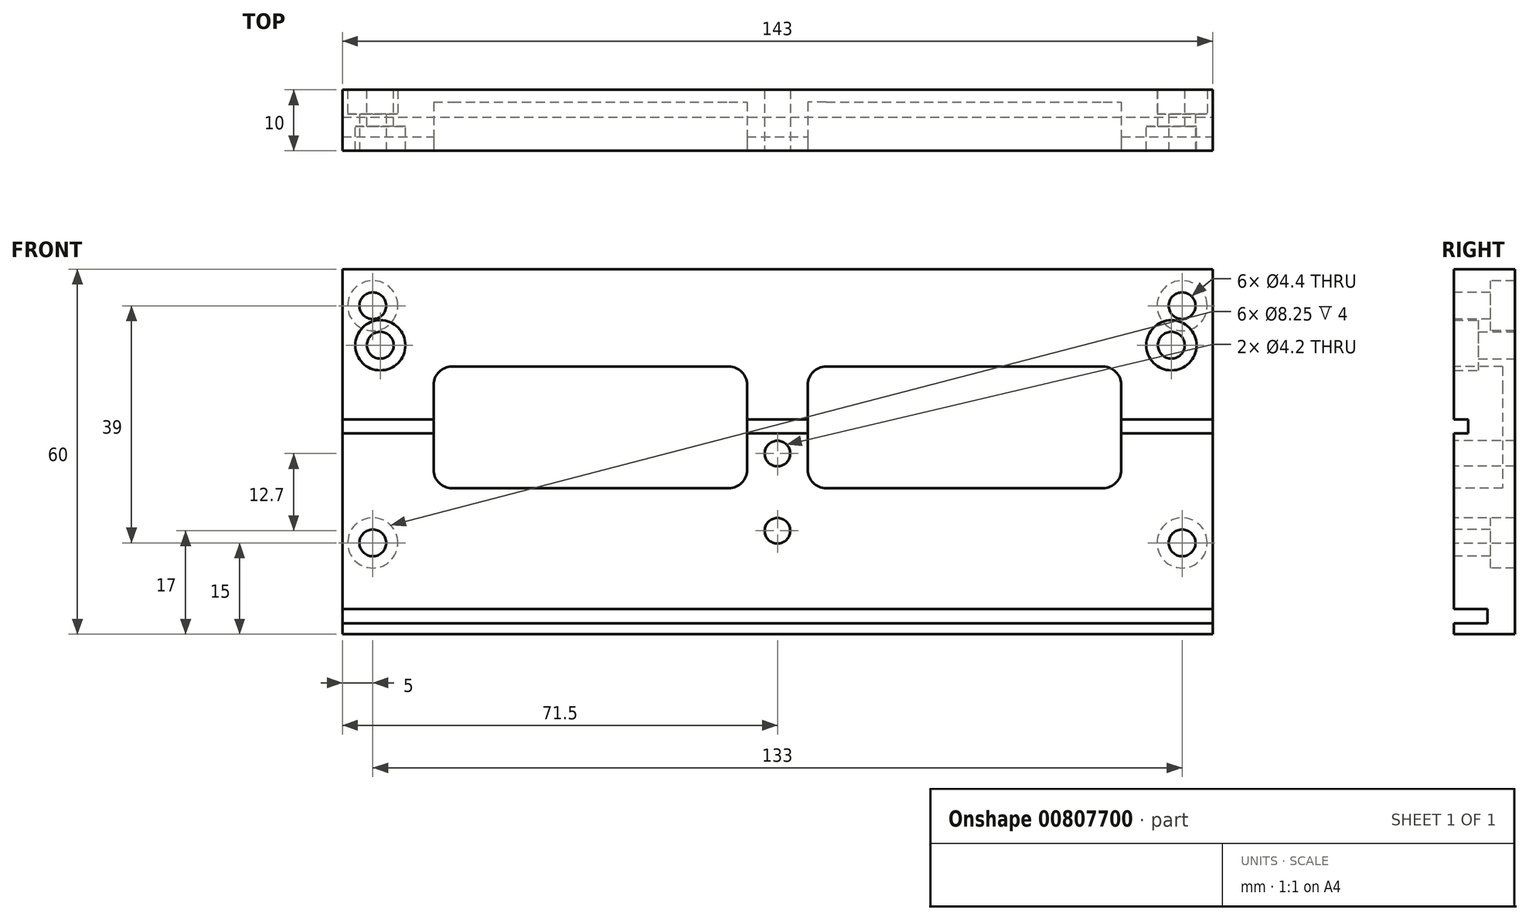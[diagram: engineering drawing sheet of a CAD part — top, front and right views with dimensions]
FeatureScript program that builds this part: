
annotation { "Feature Type Name" : "Feature", "Feature Type Description" : "" }
export const myFeature = defineFeature(function(context is Context, id is Id, definition is map)
    precondition{}
    {
        {
            var Q0;
            Q0=qCreatedBy(makeId("Front.planeOp"),FACE);
            var sketch = newSketch(context, id + "F0", { "sketchPlane" : qUnion([Q0])});
            skLineSegment(sketch, "E0.bottom", {"start": v(71.5, 30) * mm, "end": v(-71.5, 30) * mm});
            skLineSegment(sketch, "E0.top", {"start": v(71.5, -30) * mm, "end": v(-71.5, -30) * mm});
            skLineSegment(sketch, "E0.left", {"start": v(71.5, 30) * mm, "end": v(71.5, -30) * mm});
            skLineSegment(sketch, "E0.right", {"start": v(-71.5, 30) * mm, "end": v(-71.5, -30) * mm});
            skPoint(sketch, "E0.middle", {"position": v(0, 0) * mm});
            skSolve(sketch);
        }
        {
            var Q0;
            Q0 = qSketchRegion(id + "F0", true);
            extrude(context, id + "F1", {"entities" : qUnion([Q0]), "depth" : 10 * mm, "offsetDistance" : 25 * mm});
        }
        {
            var Q0;
            Q0=makeQuery(id+"F1.opExtrude","CAP_FACE",FACE,{"disambiguationData":[OSD([sQuery(id+"F0.wireOp",EDGE,"E0.bottom"),sQuery(id+"F0.wireOp",EDGE,"E0.top"),sQuery(id+"F0.wireOp",EDGE,"E0.left"),sQuery(id+"F0.wireOp",EDGE,"E0.right")])],"isStart":false});
            var sketch = newSketch(context, id + "F2", { "sketchPlane" : qUnion([Q0])});
            skLineSegment(sketch, "E1.bottom", {"start": v(-56.5, 14) * mm, "end": v(-5, 14) * mm});
            skLineSegment(sketch, "E1.top", {"start": v(-56.5, -6) * mm, "end": v(-5, -6) * mm});
            skLineSegment(sketch, "E1.left", {"start": v(-56.5, 14) * mm, "end": v(-56.5, -6) * mm});
            skLineSegment(sketch, "E1.right", {"start": v(-5, 14) * mm, "end": v(-5, -6) * mm});
            skLineSegment(sketch, "E2.bottom", {"start": v(5, 14) * mm, "end": v(56.5, 14) * mm});
            skLineSegment(sketch, "E2.top", {"start": v(5, -6) * mm, "end": v(56.5, -6) * mm});
            skLineSegment(sketch, "E2.left", {"start": v(5, 14) * mm, "end": v(5, -6) * mm});
            skLineSegment(sketch, "E2.right", {"start": v(56.5, 14) * mm, "end": v(56.5, -6) * mm});
            skPoint(sketch, "E3", {"position": v(0, -14.26) * mm});
            skPoint(sketch, "E4", {"position": v(0, 15.54) * mm});
            skSolve(sketch);
        }
        {
            var Q0;
            Q0 = qSketchRegion(id + "F2", true);
            extrude(context, id + "F3", {"entities" : qUnion([Q0]), "operationType" : NewBodyOperationType.REMOVE, "oppositeDirection" : true, "depth" : 8 * mm, "offsetDistance" : 25 * mm});
        }
        {
            var Q0;
            Q0=makeQuery(id+"F3.boolean.opBoolean","COPY",EDGE,{"derivedFrom":makeQuery(id+"F3.opExtrude","SWEPT_EDGE",EDGE,{"disambiguationData":[OSD([sQuery(id+"F2.wireOp",EDGE,"E1.bottom"),sQuery(id+"F2.wireOp",EDGE,"E1.left")])]})});
            var Q1;
            Q1=makeQuery(id+"F3.boolean.opBoolean","COPY",EDGE,{"derivedFrom":makeQuery(id+"F3.opExtrude","SWEPT_EDGE",EDGE,{"disambiguationData":[OSD([sQuery(id+"F2.wireOp",EDGE,"E1.top"),sQuery(id+"F2.wireOp",EDGE,"E1.right")])]})});
            var Q2;
            Q2=makeQuery(id+"F3.boolean.opBoolean","COPY",EDGE,{"derivedFrom":makeQuery(id+"F3.opExtrude","SWEPT_EDGE",EDGE,{"disambiguationData":[OSD([sQuery(id+"F2.wireOp",EDGE,"E2.top"),sQuery(id+"F2.wireOp",EDGE,"E2.right")])]})});
            var Q3;
            Q3=makeQuery(id+"F3.boolean.opBoolean","COPY",EDGE,{"derivedFrom":makeQuery(id+"F3.opExtrude","SWEPT_EDGE",EDGE,{"disambiguationData":[OSD([sQuery(id+"F2.wireOp",EDGE,"E1.bottom"),sQuery(id+"F2.wireOp",EDGE,"E1.right")])]})});
            var Q4;
            Q4=makeQuery(id+"F3.boolean.opBoolean","COPY",EDGE,{"derivedFrom":makeQuery(id+"F3.opExtrude","SWEPT_EDGE",EDGE,{"disambiguationData":[OSD([sQuery(id+"F2.wireOp",EDGE,"E2.bottom"),sQuery(id+"F2.wireOp",EDGE,"E2.right")])]})});
            var Q5;
            Q5=makeQuery(id+"F3.boolean.opBoolean","COPY",EDGE,{"derivedFrom":makeQuery(id+"F3.opExtrude","SWEPT_EDGE",EDGE,{"disambiguationData":[OSD([sQuery(id+"F2.wireOp",EDGE,"E1.top"),sQuery(id+"F2.wireOp",EDGE,"E1.left")])]})});
            var Q6;
            Q6=makeQuery(id+"F3.boolean.opBoolean","COPY",EDGE,{"derivedFrom":makeQuery(id+"F3.opExtrude","SWEPT_EDGE",EDGE,{"disambiguationData":[OSD([sQuery(id+"F2.wireOp",EDGE,"E2.top"),sQuery(id+"F2.wireOp",EDGE,"E2.left")])]})});
            var Q7;
            Q7=makeQuery(id+"F3.boolean.opBoolean","COPY",EDGE,{"derivedFrom":makeQuery(id+"F3.opExtrude","SWEPT_EDGE",EDGE,{"disambiguationData":[OSD([sQuery(id+"F2.wireOp",EDGE,"E2.bottom"),sQuery(id+"F2.wireOp",EDGE,"E2.left")])]})});
            fillet(context, id + "F4", {"entities" : qUnion([Q0, Q1, Q2, Q3, Q4, Q5, Q6, Q7]), "radius" : 3 * mm, "tangentPropagation" : true, "allowEdgeOverflow" : false});
        }
        {
            var Q0;
            Q0=makeQuery(id+"F1.opExtrude","CAP_FACE",FACE,{"disambiguationData":[OSD([sQuery(id+"F0.wireOp",EDGE,"E0.bottom"),sQuery(id+"F0.wireOp",EDGE,"E0.top"),sQuery(id+"F0.wireOp",EDGE,"E0.left"),sQuery(id+"F0.wireOp",EDGE,"E0.right")])],"isStart":false});
            var sketch = newSketch(context, id + "F5", { "sketchPlane" : qUnion([Q0])});
            skLineSegment(sketch, "E5.bottom", {"start": v(-71.5, -25.9) * mm, "end": v(71.5, -25.9) * mm});
            skLineSegment(sketch, "E5.top", {"start": v(-71.5, -28.2) * mm, "end": v(71.5, -28.2) * mm});
            skLineSegment(sketch, "E5.left", {"start": v(-71.5, -25.9) * mm, "end": v(-71.5, -28.2) * mm});
            skLineSegment(sketch, "E5.right", {"start": v(71.5, -25.9) * mm, "end": v(71.5, -28.2) * mm});
            skSolve(sketch);
        }
        {
            var Q0;
            Q0 = qSketchRegion(id + "F5", true);
            extrude(context, id + "F6", {"entities" : qUnion([Q0]), "operationType" : NewBodyOperationType.REMOVE, "oppositeDirection" : true, "depth" : 5.5 * mm, "offsetDistance" : 25 * mm});
        }
        {
            var Q0;
            {var subQ6=sQuery(id+"F0.wireOp",EDGE,"E0.bottom");var subQ8=sQuery(id+"F0.wireOp",EDGE,"E0.left");var subQ10=sQuery(id+"F0.wireOp",EDGE,"E0.right");Q0=makeQuery(id+"F6.boolean.opBoolean","SPLIT",FACE,{"disambiguationData":[TD([makeQuery(id+"F1.opExtrude","SWEPT_FACE",FACE,{"disambiguationData":[OSD([subQ6])]})])],"derivedFrom":makeQuery(id+"F1.opExtrude","CAP_FACE",FACE,{"disambiguationData":[OSD([subQ6,sQuery(id+"F0.wireOp",EDGE,"E0.top"),subQ8,subQ10])],"isStart":false})});}
            var sketch = newSketch(context, id + "F7", { "sketchPlane" : qUnion([Q0])});
            skLineSegment(sketch, "E6.bottom", {"start": v(-71.5, 5.3) * mm, "end": v(71.5, 5.3) * mm});
            skLineSegment(sketch, "E6.top", {"start": v(-71.5, 3) * mm, "end": v(71.5, 3) * mm});
            skLineSegment(sketch, "E6.left", {"start": v(-71.5, 5.3) * mm, "end": v(-71.5, 3) * mm});
            skLineSegment(sketch, "E6.right", {"start": v(71.5, 5.3) * mm, "end": v(71.5, 3) * mm});
            skSolve(sketch);
        }
        {
            var Q0;
            Q0 = qSketchRegion(id + "F7", true);
            extrude(context, id + "F8", {"entities" : qUnion([Q0]), "operationType" : NewBodyOperationType.REMOVE, "oppositeDirection" : true, "depth" : 2.3 * mm, "offsetDistance" : 25 * mm});
        }
        {
            var Q0;
            Q0=makeQuery(id+"F1.opExtrude","CAP_FACE",FACE,{"disambiguationData":[OSD([sQuery(id+"F0.wireOp",EDGE,"E0.bottom"),sQuery(id+"F0.wireOp",EDGE,"E0.top"),sQuery(id+"F0.wireOp",EDGE,"E0.left"),sQuery(id+"F0.wireOp",EDGE,"E0.right")])],"isStart":true});
            var sketch = newSketch(context, id + "F9", { "sketchPlane" : qUnion([Q0])});
            skPoint(sketch, "E7", {"position": v(-66.5, 24) * mm});
            skPoint(sketch, "E8", {"position": v(-66.5, -15) * mm});
            skPoint(sketch, "E9", {"position": v(66.5, -15) * mm});
            skPoint(sketch, "E10", {"position": v(66.5, 24) * mm});
            skSolve(sketch);
        }
        {
            var Q0;
            Q0=sQuery(id+"F9.wireOp",VERTEX,"E7");
            var Q1;
            Q1=sQuery(id+"F9.wireOp",VERTEX,"E8");
            var Q2;
            Q2=sQuery(id+"F9.wireOp",VERTEX,"E9");
            var Q3;
            Q3=sQuery(id+"F9.wireOp",VERTEX,"E10");
            var Q4;
            Q4=makeQuery(id+"F1.opExtrude","SWEPT_BODY",BODY,{"disambiguationData":[OSD([sQuery(id+"F0.wireOp",EDGE,"E0.bottom"),sQuery(id+"F0.wireOp",EDGE,"E0.top"),sQuery(id+"F0.wireOp",EDGE,"E0.left"),sQuery(id+"F0.wireOp",EDGE,"E0.right")])]});
            hole(context, id + "F10", {"style" : HoleStyle.C_BORE, "endStyle" : HoleEndStyle.THROUGH, "standardTappedOrClearance" : lookupTablePath({ "standard" : "ISO", "fit" : "Normal", "size" : "M4", "type" : "Clearance" }), "standardBlindInLast" : lookupTablePath({ "fit" : "Standard", "standard" : "ISO", "size" : "M4", "type" : "Clearance" }), "holeDiameter" : 4.4 * mm, "cBoreDiameter" : 8.25 * mm, "cBoreDepth" : 4 * mm, "majorDiameter" : 5 * mm, "tappedDepth" : 20 * mm, "tapClearance" : 3, "locations" : qUnion([Q0, Q1, Q2, Q3]), "scope" : qUnion([Q4]), "startStyle" : HoleStartStyle.PART});
        }
        {
            var Q0;
            {var subQ12=sQuery(id+"F0.wireOp",EDGE,"E0.bottom");var subQ13=makeQuery(id+"F1.opExtrude","SWEPT_FACE",FACE,{"disambiguationData":[OSD([subQ12])]});var subQ15=sQuery(id+"F0.wireOp",EDGE,"E0.left");var subQ18=sQuery(id+"F0.wireOp",EDGE,"E0.right");Q0=makeQuery(id+"F8.boolean.opBoolean","SPLIT",FACE,{"disambiguationData":[TD([subQ13])],"derivedFrom":makeQuery(id+"F6.boolean.opBoolean","SPLIT",FACE,{"disambiguationData":[TD([subQ13])],"derivedFrom":makeQuery(id+"F1.opExtrude","CAP_FACE",FACE,{"disambiguationData":[OSD([subQ12,sQuery(id+"F0.wireOp",EDGE,"E0.top"),subQ15,subQ18])],"isStart":false})})});}
            var sketch = newSketch(context, id + "F11", { "sketchPlane" : qUnion([Q0])});
            skPoint(sketch, "E11", {"position": v(-65.27, 17.5) * mm});
            skPoint(sketch, "E12", {"position": v(64.73, 17.5) * mm});
            skSolve(sketch);
        }
        {
            var Q0;
            Q0=sQuery(id+"F11.wireOp",VERTEX,"E11");
            var Q1;
            Q1=sQuery(id+"F11.wireOp",VERTEX,"E12");
            var Q2;
            Q2=makeQuery(id+"F1.opExtrude","SWEPT_BODY",BODY,{"disambiguationData":[OSD([sQuery(id+"F0.wireOp",EDGE,"E0.bottom"),sQuery(id+"F0.wireOp",EDGE,"E0.top"),sQuery(id+"F0.wireOp",EDGE,"E0.left"),sQuery(id+"F0.wireOp",EDGE,"E0.right")])]});
            hole(context, id + "F12", {"style" : HoleStyle.C_BORE, "endStyle" : HoleEndStyle.THROUGH, "standardTappedOrClearance" : lookupTablePath({ "standard" : "ISO", "fit" : "Normal", "size" : "M4", "type" : "Clearance" }), "standardBlindInLast" : lookupTablePath({ "fit" : "Standard", "standard" : "ISO", "size" : "M4", "type" : "Clearance" }), "holeDiameter" : 4.4 * mm, "cBoreDiameter" : 8.25 * mm, "cBoreDepth" : 4 * mm, "majorDiameter" : 5 * mm, "tappedDepth" : 20 * mm, "tapClearance" : 3, "locations" : qUnion([Q0, Q1]), "scope" : qUnion([Q2]), "startStyle" : HoleStartStyle.PART});
        }
        {
            var Q0;
            Q0=makeQuery(id+"F1.opExtrude","CAP_FACE",FACE,{"disambiguationData":[OSD([sQuery(id+"F0.wireOp",EDGE,"E0.bottom"),sQuery(id+"F0.wireOp",EDGE,"E0.top"),sQuery(id+"F0.wireOp",EDGE,"E0.left"),sQuery(id+"F0.wireOp",EDGE,"E0.right")])],"isStart":true});
            var sketch = newSketch(context, id + "F13", { "sketchPlane" : qUnion([Q0])});
            skPoint(sketch, "E13", {"position": v(0, -0.3) * mm});
            skPoint(sketch, "E14", {"position": v(0, -13) * mm});
            skSolve(sketch);
        }
        {
            var Q0;
            Q0=sQuery(id+"F13.wireOp",VERTEX,"E13");
            var Q1;
            Q1=sQuery(id+"F13.wireOp",VERTEX,"E14");
            var Q2;
            Q2=makeQuery(id+"F1.opExtrude","SWEPT_BODY",BODY,{"disambiguationData":[OSD([sQuery(id+"F0.wireOp",EDGE,"E0.bottom"),sQuery(id+"F0.wireOp",EDGE,"E0.top"),sQuery(id+"F0.wireOp",EDGE,"E0.left"),sQuery(id+"F0.wireOp",EDGE,"E0.right")])]});
            hole(context, id + "F14", {"style" : HoleStyle.SIMPLE, "endStyle" : HoleEndStyle.THROUGH, "standardTappedOrClearance" : lookupTablePath({ "standard" : "ISO", "engagement" : "75%", "pitch" : "0.8 mm", "size" : "M5", "type" : "Tapped" }), "standardBlindInLast" : lookupTablePath({ "standard" : "ISO", "engagement" : "75%", "pitch" : "0.8 mm", "size" : "M5", "type" : "Tapped" }), "holeDiameter" : 4.2 * mm, "majorDiameter" : 5 * mm, "showTappedDepth" : true, "tappedDepth" : 20 * mm, "tapClearance" : 3, "locations" : qUnion([Q0, Q1]), "scope" : qUnion([Q2]), "startStyle" : HoleStartStyle.PART});
        }
    });
